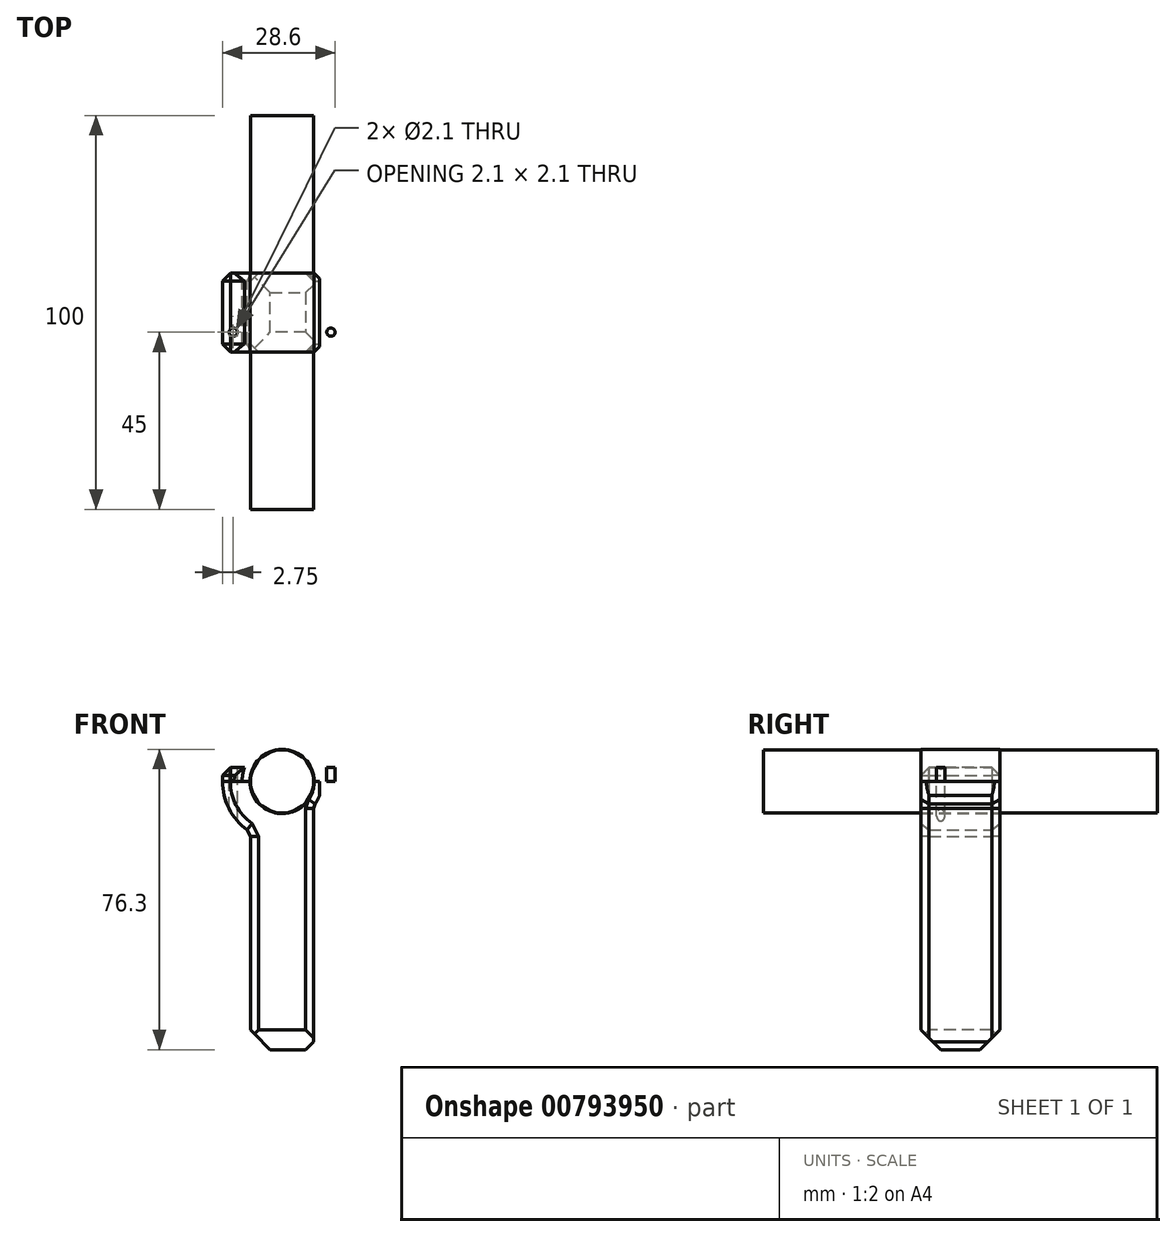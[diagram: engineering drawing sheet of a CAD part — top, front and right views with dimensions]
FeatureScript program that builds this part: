
annotation { "Feature Type Name" : "Feature", "Feature Type Description" : "" }
export const myFeature = defineFeature(function(context is Context, id is Id, definition is map)
    precondition{}
    {
        {
            var Q0;
            Q0=qCreatedBy(makeId("Front.planeOp"),FACE);
            var sketch = newSketch(context, id + "F0", { "sketchPlane" : qUnion([Q0])});
            skCircle(sketch, "E0", {"center": v(0, 0) * mm, "radius": 8 * mm});
            skSolve(sketch);
        }
        {
            var Q0;
            Q0=makeQuery(id+"F0.imprint","IMPRINT",FACE,{"disambiguationData":[TD([[makeQuery(id+"F0.imprint","IMPRINT",EDGE,{"derivedFrom":sQuery(id+"F0.wireOp",EDGE,"E0")}),1.0]])]});
            extrude(context, id + "F1", {"entities" : qUnion([Q0]), "endBound" : BoundingType.SYMMETRIC, "depth" : 100 * mm, "offsetDistance" : 25 * mm});
        }
        {
            var Q0;
            Q0=qCreatedBy(makeId("Front.planeOp"),FACE);
            var sketch = newSketch(context, id + "F2", { "sketchPlane" : qUnion([Q0])});
            skArc(sketch, "E1", {"start": v(-8.15, 0) * mm, "mid": v(0, -8.15) * mm, "end": v(8.15, 0) * mm});
            skLineSegment(sketch, "E2", {"start": v(-8.15, 0) * mm, "end": v(-15.15, 0) * mm});
            skLineSegment(sketch, "E3", {"start": v(8.15, 0) * mm, "end": v(15.15, 0) * mm});
            skLineSegment(sketch, "E4", {"start": v(-8, -6.25) * mm, "end": v(-8, -68.15) * mm});
            skLineSegment(sketch, "E5", {"start": v(-8, -68.15) * mm, "end": v(8, -68.15) * mm});
            skLineSegment(sketch, "E6", {"start": v(8, -68.15) * mm, "end": v(8, -6.25) * mm});
            skPoint(sketch, "E7", {"position": v(0, -68.15) * mm});
            skArc(sketch, "E8", {"start": v(-10.15, 0) * mm, "mid": v(0, -10.15) * mm, "end": v(10.15, 0) * mm});
            skArc(sketch, "E9", {"start": v(-15.15, 0) * mm, "mid": v(-13.24, -7.36) * mm, "end": v(-8, -12.87) * mm});
            skArc(sketch, "E10", {"start": v(15.15, 0) * mm, "mid": v(13.24, -7.36) * mm, "end": v(8, -12.87) * mm});
            skArc(sketch, "E11", {"start": v(-8.15, 0) * mm, "mid": v(0, 8.15) * mm, "end": v(8.15, 0) * mm});
            skArc(sketch, "E12", {"start": v(-10.15, 0) * mm, "mid": v(0, 10.15) * mm, "end": v(10.15, 0) * mm});
            skLineSegment(sketch, "E13", {"start": v(-15.15, 0) * mm, "end": v(-15.15, 3.5) * mm});
            skLineSegment(sketch, "E14", {"start": v(-15.15, 3.5) * mm, "end": v(-9.53, 3.5) * mm});
            skLineSegment(sketch, "E15.MirrorCS", {"start": v(15.15, 3.5) * mm, "end": v(9.53, 3.5) * mm});
            skLineSegment(sketch, "E16.MirrorCS", {"start": v(15.15, 0) * mm, "end": v(15.15, 3.5) * mm});
            skSolve(sketch);
        }
        {
            var Q0;
            {var subQ0=sQuery(id+"F2.wireOp",EDGE,"E9");Q0=makeQuery(id+"F2.imprint","IMPRINT",FACE,{"disambiguationData":[TD([[makeQuery(id+"F2.imprint","IMPRINT",EDGE,{"derivedFrom":subQ0}),1.0]])]});}
            var Q1;
            {var subQ2=sQuery(id+"F2.wireOp",EDGE,"E1");Q1=makeQuery(id+"F2.imprint","IMPRINT",FACE,{"disambiguationData":[TD([[makeQuery(id+"F2.imprint","IMPRINT",EDGE,{"derivedFrom":subQ2}),-1.0]])]});}
            var Q2;
            {var subQ1=sQuery(id+"F2.wireOp",EDGE,"E5");Q2=makeQuery(id+"F2.imprint","IMPRINT",FACE,{"disambiguationData":[TD([[makeQuery(id+"F2.imprint","IMPRINT",EDGE,{"derivedFrom":subQ1}),1.0]])]});}
            var Q3;
            {var subQ0=sQuery(id+"F2.wireOp",EDGE,"E10");Q3=makeQuery(id+"F2.imprint","IMPRINT",FACE,{"disambiguationData":[TD([[makeQuery(id+"F2.imprint","IMPRINT",EDGE,{"derivedFrom":subQ0}),-1.0]])]});}
            extrude(context, id + "F3", {"entities" : qUnion([Q0, Q1, Q2, Q3]), "endBound" : BoundingType.SYMMETRIC, "depth" : 20 * mm, "offsetDistance" : 25 * mm});
        }
        {
            var Q0;
            {var subQ0=sQuery(id+"F2.wireOp",EDGE,"E11");Q0=makeQuery(id+"F2.imprint","IMPRINT",FACE,{"disambiguationData":[TD([[makeQuery(id+"F2.imprint","IMPRINT",EDGE,{"derivedFrom":subQ0}),1.0]])]});}
            var Q1;
            {var subQ4=sQuery(id+"F2.wireOp",EDGE,"E15.MirrorCS");Q1=makeQuery(id+"F2.imprint","IMPRINT",FACE,{"disambiguationData":[TD([[makeQuery(id+"F2.imprint","IMPRINT",EDGE,{"derivedFrom":subQ4}),1.0]])]});}
            var Q2;
            {var subQ0=sQuery(id+"F2.wireOp",EDGE,"E13");Q2=makeQuery(id+"F2.imprint","IMPRINT",FACE,{"disambiguationData":[TD([[makeQuery(id+"F2.imprint","IMPRINT",EDGE,{"derivedFrom":subQ0}),-1.0]])]});}
            extrude(context, id + "F4", {"entities" : qUnion([Q0, Q1, Q2]), "endBound" : BoundingType.SYMMETRIC, "depth" : 20 * mm, "offsetDistance" : 25 * mm});
        }
        {
            var Q0;
            Q0=makeQuery(id+"F4.opExtrude","SWEPT_FACE",FACE,{"disambiguationData":[OSD([sQuery(id+"F2.wireOp",EDGE,"E15.MirrorCS")])]});
            var sketch = newSketch(context, id + "F5", { "sketchPlane" : qUnion([Q0])});
            skCircle(sketch, "E17", {"center": v(12.4, 5) * mm, "radius": 1.05 * mm});
            skCircle(sketch, "E18.MirrorC", {"center": v(12.4, -5) * mm, "radius": 1.05 * mm});
            skCircle(sketch, "E19.MirrorC", {"center": v(-12.4, 5) * mm, "radius": 1.05 * mm});
            skCircle(sketch, "E20.MirrorC", {"center": v(-12.4, -5) * mm, "radius": 1.05 * mm});
            skSolve(sketch);
        }
        {
            var Q0;
            Q0=makeQuery(id+"F5.imprint","IMPRINT",FACE,{"disambiguationData":[TD([[makeQuery(id+"F5.imprint","IMPRINT",EDGE,{"derivedFrom":sQuery(id+"F5.wireOp",EDGE,"E19.MirrorC")}),-1.0]])]});
            var Q1;
            Q1=makeQuery(id+"F5.imprint","IMPRINT",FACE,{"disambiguationData":[TD([[makeQuery(id+"F5.imprint","IMPRINT",EDGE,{"derivedFrom":sQuery(id+"F5.wireOp",EDGE,"E20.MirrorC")}),1.0]])]});
            var Q2;
            Q2=makeQuery(id+"F5.imprint","IMPRINT",FACE,{"disambiguationData":[TD([[makeQuery(id+"F5.imprint","IMPRINT",EDGE,{"derivedFrom":sQuery(id+"F5.wireOp",EDGE,"E17")}),1.0]])]});
            var Q3;
            Q3=makeQuery(id+"F5.imprint","IMPRINT",FACE,{"disambiguationData":[TD([[makeQuery(id+"F5.imprint","IMPRINT",EDGE,{"derivedFrom":sQuery(id+"F5.wireOp",EDGE,"E18.MirrorC")}),-1.0]])]});
            extrude(context, id + "F6", {"entities" : qUnion([Q0, Q1, Q2, Q3]), "operationType" : NewBodyOperationType.REMOVE, "endBound" : BoundingType.SYMMETRIC, "oppositeDirection" : true, "depth" : 50 * mm, "offsetDistance" : 25 * mm});
        }
        {
            var Q0;
            Q0=makeQuery(id+"F3.opExtrude","CAP_EDGE",EDGE,{"disambiguationData":[OSD([sQuery(id+"F2.wireOp",EDGE,"E9")])],"isStart":false});
            var Q1;
            Q1=makeQuery(id+"F3.opExtrude","CAP_EDGE",EDGE,{"disambiguationData":[OSD([sQuery(id+"F2.wireOp",EDGE,"E4")])],"isStart":false});
            var Q2;
            Q2=makeQuery(id+"F3.opExtrude","CAP_EDGE",EDGE,{"disambiguationData":[OSD([sQuery(id+"F2.wireOp",EDGE,"E6")])],"isStart":false});
            var Q3;
            Q3=makeQuery(id+"F3.opExtrude","CAP_EDGE",EDGE,{"disambiguationData":[OSD([sQuery(id+"F2.wireOp",EDGE,"E4")])],"isStart":true});
            var Q4;
            Q4=makeQuery(id+"F3.opExtrude","SWEPT_EDGE",EDGE,{"disambiguationData":[OSD([sQuery(id+"F2.wireOp",EDGE,"E4"),sQuery(id+"F2.wireOp",EDGE,"E9")])]});
            var Q5;
            Q5=makeQuery(id+"F3.opExtrude","CAP_EDGE",EDGE,{"disambiguationData":[OSD([sQuery(id+"F2.wireOp",EDGE,"E10")])],"isStart":true});
            var Q6;
            Q6=makeQuery(id+"F3.opExtrude","CAP_EDGE",EDGE,{"disambiguationData":[OSD([sQuery(id+"F2.wireOp",EDGE,"E6")])],"isStart":true});
            var Q7;
            Q7=makeQuery(id+"F3.opExtrude","SWEPT_EDGE",EDGE,{"disambiguationData":[OSD([sQuery(id+"F2.wireOp",EDGE,"E6"),sQuery(id+"F2.wireOp",EDGE,"E10")])]});
            var Q8;
            Q8=makeQuery(id+"F4.opExtrude","CAP_EDGE",EDGE,{"disambiguationData":[OSD([sQuery(id+"F2.wireOp",EDGE,"E12")])],"isStart":false});
            var Q9;
            Q9=makeQuery(id+"F4.opExtrude","CAP_EDGE",EDGE,{"disambiguationData":[OSD([sQuery(id+"F2.wireOp",EDGE,"E12")])],"isStart":true});
            var Q10;
            Q10=makeQuery(id+"F4.opExtrude","CAP_EDGE",EDGE,{"disambiguationData":[OSD([sQuery(id+"F2.wireOp",EDGE,"E13")])],"isStart":true});
            var Q11;
            Q11=makeQuery(id+"F4.opExtrude","CAP_EDGE",EDGE,{"disambiguationData":[OSD([sQuery(id+"F2.wireOp",EDGE,"E16.MirrorCS")])],"isStart":true});
            var Q12;
            Q12=makeQuery(id+"F4.opExtrude","CAP_EDGE",EDGE,{"disambiguationData":[OSD([sQuery(id+"F2.wireOp",EDGE,"E16.MirrorCS")])],"isStart":false});
            var Q13;
            Q13=makeQuery(id+"F4.opExtrude","CAP_EDGE",EDGE,{"disambiguationData":[OSD([sQuery(id+"F2.wireOp",EDGE,"E13")])],"isStart":false});
            var Q14;
            Q14=makeQuery(id+"F4.opExtrude","SWEPT_EDGE",EDGE,{"disambiguationData":[OSD([sQuery(id+"F2.wireOp",EDGE,"E13"),sQuery(id+"F2.wireOp",EDGE,"E14")])]});
            var Q15;
            Q15=makeQuery(id+"F4.opExtrude","SWEPT_EDGE",EDGE,{"disambiguationData":[OSD([sQuery(id+"F2.wireOp",EDGE,"E15.MirrorCS"),sQuery(id+"F2.wireOp",EDGE,"E16.MirrorCS")])]});
            var Q16;
            Q16=makeQuery(id+"F4.opExtrude","CAP_EDGE",EDGE,{"disambiguationData":[OSD([sQuery(id+"F2.wireOp",EDGE,"E15.MirrorCS")])],"isStart":false});
            var Q17;
            Q17=makeQuery(id+"F4.opExtrude","CAP_EDGE",EDGE,{"disambiguationData":[OSD([sQuery(id+"F2.wireOp",EDGE,"E15.MirrorCS")])],"isStart":true});
            var Q18;
            Q18=makeQuery(id+"F4.opExtrude","CAP_EDGE",EDGE,{"disambiguationData":[OSD([sQuery(id+"F2.wireOp",EDGE,"E14")])],"isStart":true});
            var Q19;
            Q19=makeQuery(id+"F4.opExtrude","CAP_EDGE",EDGE,{"disambiguationData":[OSD([sQuery(id+"F2.wireOp",EDGE,"E14")])],"isStart":false});
            chamfer(context, id + "F7", {"entities" : qUnion([Q0, Q1, Q2, Q3, Q4, Q5, Q6, Q7, Q8, Q9, Q10, Q11, Q12, Q13, Q14, Q15, Q16, Q17, Q18, Q19]), "width" : 2 * mm, "tangentPropagation" : true});
        }
        {
            var Q0;
            Q0=makeQuery(id+"F3.opExtrude","SWEPT_EDGE",EDGE,{"disambiguationData":[OSD([sQuery(id+"F2.wireOp",EDGE,"E4"),sQuery(id+"F2.wireOp",EDGE,"E5")])]});
            var Q1;
            Q1=makeQuery(id+"F3.opExtrude","CAP_EDGE",EDGE,{"disambiguationData":[OSD([sQuery(id+"F2.wireOp",EDGE,"E5")])],"isStart":true});
            var Q2;
            Q2=makeQuery(id+"F3.opExtrude","SWEPT_EDGE",EDGE,{"disambiguationData":[OSD([sQuery(id+"F2.wireOp",EDGE,"E5"),sQuery(id+"F2.wireOp",EDGE,"E6")])]});
            var Q3;
            Q3=makeQuery(id+"F3.opExtrude","CAP_EDGE",EDGE,{"disambiguationData":[OSD([sQuery(id+"F2.wireOp",EDGE,"E5")])],"isStart":false});
            chamfer(context, id + "F8", {"entities" : qUnion([Q0, Q1, Q2, Q3]), "width" : 5 * mm, "tangentPropagation" : true});
        }
    });
